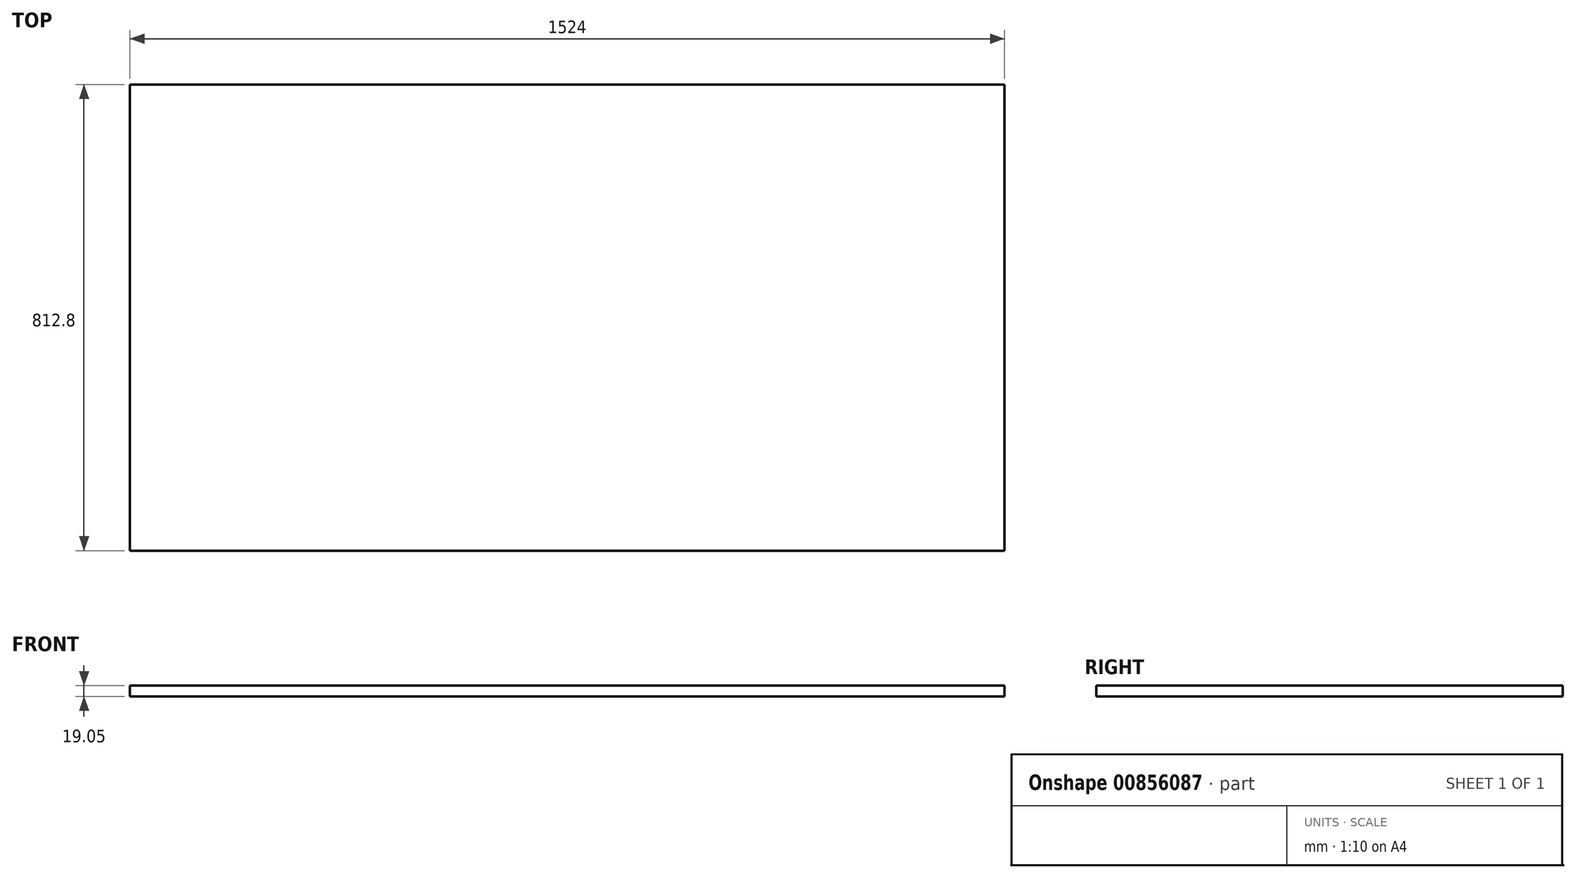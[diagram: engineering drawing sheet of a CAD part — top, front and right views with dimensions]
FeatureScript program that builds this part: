
annotation { "Feature Type Name" : "Feature", "Feature Type Description" : "" }
export const myFeature = defineFeature(function(context is Context, id is Id, definition is map)
    precondition{}
    {
        {
            var Q0;
            Q0=qCreatedBy(makeId("Top.planeOp"),FACE);
            var sketch = newSketch(context, id + "F0", { "sketchPlane" : qUnion([Q0])});
            skLineSegment(sketch, "E0.bottom", {"start": v(762, 406.4) * mm, "end": v(-762, 406.4) * mm});
            skLineSegment(sketch, "E0.top", {"start": v(762, -406.4) * mm, "end": v(-762, -406.4) * mm});
            skLineSegment(sketch, "E0.left", {"start": v(762, 406.4) * mm, "end": v(762, -406.4) * mm});
            skLineSegment(sketch, "E0.right", {"start": v(-762, 406.4) * mm, "end": v(-762, -406.4) * mm});
            skPoint(sketch, "E0.middle", {"position": v(0, 0) * mm});
            skLineSegment(sketch, "E1.0", {"start": v(596.9, -355.6) * mm, "end": v(-596.9, -355.6) * mm});
            skLineSegment(sketch, "E2.0", {"start": v(-596.9, 254) * mm, "end": v(-596.9, -368.3) * mm});
            skLineSegment(sketch, "E3.0", {"start": v(596.9, 254) * mm, "end": v(-596.9, 254) * mm});
            skLineSegment(sketch, "E4.0", {"start": v(596.9, 254) * mm, "end": v(596.9, -355.6) * mm});
            skSolve(sketch);
        }
        {
            var Q0;
            {var subQ0=sQuery(id+"F0.wireOp",EDGE,"E1.0");var subQ1=sQuery(id+"F0.wireOp",EDGE,"1e663299-5a7d-40fe-bcb3-75d561153807.0");var subQ2=makeQuery(id+"F0.imprint","INTERSECT",VERTEX,{"derivedFrom":[subQ1,subQ0]});Q0=makeQuery(id+"F0.imprint","IMPRINT",FACE,{"disambiguationData":[TD([[makeQuery(id+"F0.imprint","IMPRINT",EDGE,{"disambiguationData":[TD([[subQ2,-1.0]])],"derivedFrom":subQ1}),-1.0]])]});}
            var Q1;
            {var subQ0=sQuery(id+"F0.wireOp",EDGE,"E2.0");var subQ1=sQuery(id+"F0.wireOp",EDGE,"bf833f17-78a2-4387-89d4-3cf227528ae4.0");var subQ2=makeQuery(id+"F0.imprint","INTERSECT",VERTEX,{"derivedFrom":[subQ1,subQ0]});Q1=makeQuery(id+"F0.imprint","IMPRINT",FACE,{"disambiguationData":[TD([[makeQuery(id+"F0.imprint","IMPRINT",EDGE,{"disambiguationData":[TD([[subQ2,-1.0]])],"derivedFrom":subQ1}),1.0]])]});}
            var Q2;
            {var subQ0=sQuery(id+"F0.wireOp",EDGE,"E1.0");var subQ1=sQuery(id+"F0.wireOp",EDGE,"E0.left");var subQ2=makeQuery(id+"F0.imprint","INTERSECT",VERTEX,{"derivedFrom":[subQ1,subQ0]});Q2=makeQuery(id+"F0.imprint","IMPRINT",FACE,{"disambiguationData":[TD([[makeQuery(id+"F0.imprint","IMPRINT",EDGE,{"disambiguationData":[TD([[subQ2,1.0]])],"derivedFrom":subQ1}),-1.0]])]});}
            var Q3;
            {var subQ0=sQuery(id+"F0.wireOp",EDGE,"E2.0");var subQ1=sQuery(id+"F0.wireOp",EDGE,"E0.top");var subQ2=makeQuery(id+"F0.imprint","INTERSECT",VERTEX,{"derivedFrom":[subQ1,subQ0]});Q3=makeQuery(id+"F0.imprint","IMPRINT",FACE,{"disambiguationData":[TD([[makeQuery(id+"F0.imprint","IMPRINT",EDGE,{"disambiguationData":[TD([[subQ2,1.0]])],"derivedFrom":subQ1}),-1.0]])]});}
            var Q4;
            {var subQ0=sQuery(id+"F0.wireOp",EDGE,"E3.0");var subQ1=sQuery(id+"F0.wireOp",EDGE,"1e663299-5a7d-40fe-bcb3-75d561153807.0");var subQ2=makeQuery(id+"F0.imprint","INTERSECT",VERTEX,{"derivedFrom":[subQ1,subQ0]});Q4=makeQuery(id+"F0.imprint","IMPRINT",FACE,{"disambiguationData":[TD([[makeQuery(id+"F0.imprint","IMPRINT",EDGE,{"disambiguationData":[TD([[subQ2,-1.0]])],"derivedFrom":subQ1}),-1.0]])]});}
            var Q5;
            {var subQ0=sQuery(id+"F0.wireOp",EDGE,"E2.0");var subQ1=sQuery(id+"F0.wireOp",EDGE,"E0.bottom");var subQ2=makeQuery(id+"F0.imprint","INTERSECT",VERTEX,{"derivedFrom":[subQ1,subQ0]});Q5=makeQuery(id+"F0.imprint","IMPRINT",FACE,{"disambiguationData":[TD([[makeQuery(id+"F0.imprint","IMPRINT",EDGE,{"disambiguationData":[TD([[subQ2,1.0]])],"derivedFrom":subQ1}),1.0]])]});}
            var Q6;
            {var subQ0=sQuery(id+"F0.wireOp",EDGE,"E4.0");var subQ1=sQuery(id+"F0.wireOp",EDGE,"bf833f17-78a2-4387-89d4-3cf227528ae4.0");var subQ2=makeQuery(id+"F0.imprint","INTERSECT",VERTEX,{"derivedFrom":[subQ1,subQ0]});Q6=makeQuery(id+"F0.imprint","IMPRINT",FACE,{"disambiguationData":[TD([[makeQuery(id+"F0.imprint","IMPRINT",EDGE,{"disambiguationData":[TD([[subQ2,-1.0]])],"derivedFrom":subQ1}),1.0]])]});}
            var Q7;
            {var subQ0=sQuery(id+"F0.wireOp",EDGE,"E4.0");var subQ1=sQuery(id+"F0.wireOp",EDGE,"E1.0");var subQ2=makeQuery(id+"F0.imprint","INTERSECT",VERTEX,{"derivedFrom":[subQ1,subQ0]});Q7=makeQuery(id+"F0.imprint","IMPRINT",FACE,{"disambiguationData":[TD([[makeQuery(id+"F0.imprint","IMPRINT",EDGE,{"disambiguationData":[TD([[subQ2,-1.0]])],"derivedFrom":subQ1}),-1.0]])]});}
            var Q8;
            {var subQ0=sQuery(id+"F0.wireOp",EDGE,"E0.right");var subQ1=sQuery(id+"F0.wireOp",EDGE,"E0.bottom");var subQ2=makeQuery(id+"F0.imprint","INTERSECT",VERTEX,{"derivedFrom":[subQ1,subQ0]});Q8=makeQuery(id+"F0.imprint","IMPRINT",FACE,{"disambiguationData":[TD([[makeQuery(id+"F0.imprint","IMPRINT",EDGE,{"disambiguationData":[TD([[subQ2,1.0]])],"derivedFrom":subQ1}),1.0]])]});}
            var Q9;
            {var subQ0=sQuery(id+"F0.wireOp",EDGE,"E3.0");var subQ1=sQuery(id+"F0.wireOp",EDGE,"c6801c2d-4655-43d8-bb48-015dadecdbf6.0");var subQ2=makeQuery(id+"F0.imprint","INTERSECT",VERTEX,{"derivedFrom":[subQ1,subQ0]});Q9=makeQuery(id+"F0.imprint","IMPRINT",FACE,{"disambiguationData":[TD([[makeQuery(id+"F0.imprint","IMPRINT",EDGE,{"disambiguationData":[TD([[subQ2,-1.0]])],"derivedFrom":subQ1}),1.0]])]});}
            var Q10;
            {var subQ0=sQuery(id+"F0.wireOp",EDGE,"E1.0");var subQ1=sQuery(id+"F0.wireOp",EDGE,"c6801c2d-4655-43d8-bb48-015dadecdbf6.0");var subQ2=makeQuery(id+"F0.imprint","INTERSECT",VERTEX,{"derivedFrom":[subQ1,subQ0]});Q10=makeQuery(id+"F0.imprint","IMPRINT",FACE,{"disambiguationData":[TD([[makeQuery(id+"F0.imprint","IMPRINT",EDGE,{"disambiguationData":[TD([[subQ2,-1.0]])],"derivedFrom":subQ1}),1.0]])]});}
            var Q11;
            {var subQ0=sQuery(id+"F0.wireOp",EDGE,"E1.0");var subQ1=sQuery(id+"F0.wireOp",EDGE,"E0.right");var subQ2=makeQuery(id+"F0.imprint","INTERSECT",VERTEX,{"derivedFrom":[subQ1,subQ0]});Q11=makeQuery(id+"F0.imprint","IMPRINT",FACE,{"disambiguationData":[TD([[makeQuery(id+"F0.imprint","IMPRINT",EDGE,{"disambiguationData":[TD([[subQ2,1.0]])],"derivedFrom":subQ1}),1.0]])]});}
            var Q12;
            {var subQ0=sQuery(id+"F0.wireOp",EDGE,"E0.left");var subQ1=sQuery(id+"F0.wireOp",EDGE,"E0.bottom");var subQ2=makeQuery(id+"F0.imprint","INTERSECT",VERTEX,{"derivedFrom":[subQ1,subQ0]});Q12=makeQuery(id+"F0.imprint","IMPRINT",FACE,{"disambiguationData":[TD([[makeQuery(id+"F0.imprint","IMPRINT",EDGE,{"disambiguationData":[TD([[subQ2,-1.0]])],"derivedFrom":subQ1}),1.0]])]});}
            var Q13;
            {var subQ0=sQuery(id+"F0.wireOp",EDGE,"aeacb137-58dd-497a-b8ec-61548c280907.0");var subQ1=sQuery(id+"F0.wireOp",EDGE,"E0.right");var subQ2=makeQuery(id+"F0.imprint","INTERSECT",VERTEX,{"derivedFrom":[subQ1,subQ0]});Q13=makeQuery(id+"F0.imprint","IMPRINT",FACE,{"disambiguationData":[TD([[makeQuery(id+"F0.imprint","IMPRINT",EDGE,{"disambiguationData":[TD([[subQ2,1.0]])],"derivedFrom":subQ1}),1.0]])]});}
            var Q14;
            {var subQ0=sQuery(id+"F0.wireOp",EDGE,"E4.0");var subQ1=sQuery(id+"F0.wireOp",EDGE,"aeacb137-58dd-497a-b8ec-61548c280907.0");var subQ2=makeQuery(id+"F0.imprint","INTERSECT",VERTEX,{"derivedFrom":[subQ1,subQ0]});Q14=makeQuery(id+"F0.imprint","IMPRINT",FACE,{"disambiguationData":[TD([[makeQuery(id+"F0.imprint","IMPRINT",EDGE,{"disambiguationData":[TD([[subQ2,-1.0]])],"derivedFrom":subQ1}),-1.0]])]});}
            var Q15;
            {var subQ0=sQuery(id+"F0.wireOp",EDGE,"E0.right");var subQ1=sQuery(id+"F0.wireOp",EDGE,"E0.top");var subQ2=makeQuery(id+"F0.imprint","INTERSECT",VERTEX,{"derivedFrom":[subQ1,subQ0]});Q15=makeQuery(id+"F0.imprint","IMPRINT",FACE,{"disambiguationData":[TD([[makeQuery(id+"F0.imprint","IMPRINT",EDGE,{"disambiguationData":[TD([[subQ2,1.0]])],"derivedFrom":subQ1}),-1.0]])]});}
            var Q16;
            {var subQ0=sQuery(id+"F0.wireOp",EDGE,"1e663299-5a7d-40fe-bcb3-75d561153807.0");var subQ1=sQuery(id+"F0.wireOp",EDGE,"bf833f17-78a2-4387-89d4-3cf227528ae4.0");var subQ2=makeQuery(id+"F0.imprint","INTERSECT",VERTEX,{"derivedFrom":[subQ1,subQ0]});Q16=makeQuery(id+"F0.imprint","IMPRINT",FACE,{"disambiguationData":[TD([[makeQuery(id+"F0.imprint","IMPRINT",EDGE,{"disambiguationData":[TD([[subQ2,-1.0]])],"derivedFrom":subQ1}),1.0]])]});}
            var Q17;
            {var subQ0=sQuery(id+"F0.wireOp",EDGE,"bf833f17-78a2-4387-89d4-3cf227528ae4.0");var subQ1=sQuery(id+"F0.wireOp",EDGE,"E0.left");var subQ2=makeQuery(id+"F0.imprint","INTERSECT",VERTEX,{"derivedFrom":[subQ1,subQ0]});Q17=makeQuery(id+"F0.imprint","IMPRINT",FACE,{"disambiguationData":[TD([[makeQuery(id+"F0.imprint","IMPRINT",EDGE,{"disambiguationData":[TD([[subQ2,-1.0]])],"derivedFrom":subQ1}),-1.0]])]});}
            var Q18;
            {var subQ0=sQuery(id+"F0.wireOp",EDGE,"c6801c2d-4655-43d8-bb48-015dadecdbf6.0");var subQ1=sQuery(id+"F0.wireOp",EDGE,"E0.bottom");var subQ2=makeQuery(id+"F0.imprint","INTERSECT",VERTEX,{"derivedFrom":[subQ1,subQ0]});Q18=makeQuery(id+"F0.imprint","IMPRINT",FACE,{"disambiguationData":[TD([[makeQuery(id+"F0.imprint","IMPRINT",EDGE,{"disambiguationData":[TD([[subQ2,1.0]])],"derivedFrom":subQ1}),1.0]])]});}
            var Q19;
            {var subQ0=sQuery(id+"F0.wireOp",EDGE,"1e663299-5a7d-40fe-bcb3-75d561153807.0");var subQ1=sQuery(id+"F0.wireOp",EDGE,"E0.top");var subQ2=makeQuery(id+"F0.imprint","INTERSECT",VERTEX,{"derivedFrom":[subQ1,subQ0]});Q19=makeQuery(id+"F0.imprint","IMPRINT",FACE,{"disambiguationData":[TD([[makeQuery(id+"F0.imprint","IMPRINT",EDGE,{"disambiguationData":[TD([[subQ2,-1.0]])],"derivedFrom":subQ1}),-1.0]])]});}
            var Q20;
            {var subQ0=sQuery(id+"F0.wireOp",EDGE,"bf833f17-78a2-4387-89d4-3cf227528ae4.0");var subQ1=sQuery(id+"F0.wireOp",EDGE,"E0.right");var subQ2=makeQuery(id+"F0.imprint","INTERSECT",VERTEX,{"derivedFrom":[subQ1,subQ0]});Q20=makeQuery(id+"F0.imprint","IMPRINT",FACE,{"disambiguationData":[TD([[makeQuery(id+"F0.imprint","IMPRINT",EDGE,{"disambiguationData":[TD([[subQ2,-1.0]])],"derivedFrom":subQ1}),1.0]])]});}
            var Q21;
            {var subQ0=sQuery(id+"F0.wireOp",EDGE,"c6801c2d-4655-43d8-bb48-015dadecdbf6.0");var subQ1=sQuery(id+"F0.wireOp",EDGE,"E0.top");var subQ2=makeQuery(id+"F0.imprint","INTERSECT",VERTEX,{"derivedFrom":[subQ1,subQ0]});Q21=makeQuery(id+"F0.imprint","IMPRINT",FACE,{"disambiguationData":[TD([[makeQuery(id+"F0.imprint","IMPRINT",EDGE,{"disambiguationData":[TD([[subQ2,1.0]])],"derivedFrom":subQ1}),-1.0]])]});}
            var Q22;
            {var subQ0=sQuery(id+"F0.wireOp",EDGE,"E0.left");var subQ1=sQuery(id+"F0.wireOp",EDGE,"E0.top");var subQ2=makeQuery(id+"F0.imprint","INTERSECT",VERTEX,{"derivedFrom":[subQ1,subQ0]});Q22=makeQuery(id+"F0.imprint","IMPRINT",FACE,{"disambiguationData":[TD([[makeQuery(id+"F0.imprint","IMPRINT",EDGE,{"disambiguationData":[TD([[subQ2,-1.0]])],"derivedFrom":subQ1}),-1.0]])]});}
            var Q23;
            {var subQ0=sQuery(id+"F0.wireOp",EDGE,"1e663299-5a7d-40fe-bcb3-75d561153807.0");var subQ1=sQuery(id+"F0.wireOp",EDGE,"E0.bottom");var subQ2=makeQuery(id+"F0.imprint","INTERSECT",VERTEX,{"derivedFrom":[subQ1,subQ0]});Q23=makeQuery(id+"F0.imprint","IMPRINT",FACE,{"disambiguationData":[TD([[makeQuery(id+"F0.imprint","IMPRINT",EDGE,{"disambiguationData":[TD([[subQ2,-1.0]])],"derivedFrom":subQ1}),1.0]])]});}
            var Q24;
            {var subQ0=sQuery(id+"F0.wireOp",EDGE,"aeacb137-58dd-497a-b8ec-61548c280907.0");var subQ1=sQuery(id+"F0.wireOp",EDGE,"E0.left");var subQ2=makeQuery(id+"F0.imprint","INTERSECT",VERTEX,{"derivedFrom":[subQ1,subQ0]});Q24=makeQuery(id+"F0.imprint","IMPRINT",FACE,{"disambiguationData":[TD([[makeQuery(id+"F0.imprint","IMPRINT",EDGE,{"disambiguationData":[TD([[subQ2,1.0]])],"derivedFrom":subQ1}),-1.0]])]});}
            extrude(context, id + "F1", {"entities" : qUnion([Q0, Q1, Q2, Q3, Q4, Q5, Q6, Q7, Q8, Q9, Q10, Q11, Q12, Q13, Q14, Q15, Q16, Q17, Q18, Q19, Q20, Q21, Q22, Q23, Q24]), "oppositeDirection" : true, "depth" : 19.05 * mm, "offsetDistance" : 25.4 * mm});
        }
    });
